# Revit family: Hafa Shower corner IglooPro Corner all sizes
name_source: partatom
category: Generic Models
units: mm (PartAtom-declared; Revit-internal decimal feet)

## family parameters
Always vertical = Yes
Can host rebar = No
Cut with Voids When Loaded = No
Part Type = Normal
Room Calculation Point = No
Round Connector Dimension = Use Diameter
Shared = No
Work Plane-Based = No

## types (32) — shared parameters
Description = Shower corner
ETIM class = EC010034
Manufacturer = Hafa Bathroom Group
Profile and Handle material = Aluminium
URL = https://www.hafa.se

## per-type parameters (varying)
| type | Doorblade length | Doorblade width | Glass Type | Length | Width |
| 1450411 IglooPro Corner 90x90 Clear | 816 mm | 816 mm | Glass Clear | 900 mm  [stored 2.95276 ft] | 900 mm  [stored 2.95276 ft] |
| 1450410 IglooPro Corner 80x80 Clear | 716 mm | 716 mm | Glass Clear | 800 mm  [stored 2.62467 ft] | 800 mm  [stored 2.62467 ft] |
| 1450430 IglooPro Corner 70x70 Clear | 616 mm | 616 mm | Glass Clear | 700 mm  [stored 2.29659 ft] | 700 mm  [stored 2.29659 ft] |
| 1450431 IglooPro Corner 70x80 Clear | 616 mm | 716 mm | Glass Clear | 700 mm  [stored 2.29659 ft] | 800 mm  [stored 2.62467 ft] |
| 1450431 IglooPro Corner 80x70 Clear | 716 mm | 616 mm | Glass Clear | 800 mm  [stored 2.62467 ft] | 700 mm  [stored 2.29659 ft] |
| 1450432 IglooPro Corner 70x90 Clear | 816 mm | 616 mm | Glass Clear | 900 mm  [stored 2.95276 ft] | 700 mm  [stored 2.29659 ft] |
| 1450432 IglooPro Corner 90x70 Clear | 616 mm | 816 mm | Glass Clear | 700 mm  [stored 2.29659 ft] | 900 mm  [stored 2.95276 ft] |
| 1450433 IglooPro Corner 70x100 Clear | 616 mm | 916 mm  [stored 3.00525 ft] | Glass Clear | 700 mm  [stored 2.29659 ft] | 1000 mm  [stored 3.28084 ft] |
| 1450433 IglooPro Corner 100x70 Clear | 916 mm  [stored 3.00525 ft] | 616 mm | Glass Clear | 1000 mm  [stored 3.28084 ft] | 700 mm  [stored 2.29659 ft] |
| 1450434 IglooPro Corner 80x90 Clear | 716 mm | 816 mm | Glass Clear | 800 mm  [stored 2.62467 ft] | 900 mm  [stored 2.95276 ft] |
| 1450434 IglooPro Corner 90x80 Clear | 816 mm | 716 mm | Glass Clear | 900 mm  [stored 2.95276 ft] | 800 mm  [stored 2.62467 ft] |
| 1450435 IglooPro Corner 80x100 Clear | 716 mm | 916 mm  [stored 3.00525 ft] | Glass Clear | 800 mm  [stored 2.62467 ft] | 1000 mm  [stored 3.28084 ft] |
| 1450435 IglooPro Corner 100x80 Clear | 916 mm  [stored 3.00525 ft] | 716 mm | Glass Clear | 1000 mm  [stored 3.28084 ft] | 800 mm  [stored 2.62467 ft] |
| 1450436 IglooPro Corner 90x100 Clear | 816 mm | 916 mm  [stored 3.00525 ft] | Glass Clear | 900 mm  [stored 2.95276 ft] | 1000 mm  [stored 3.28084 ft] |
| 1450436 IglooPro Corner 100x90 Clear | 916 mm  [stored 3.00525 ft] | 816 mm | Glass Clear | 1000 mm  [stored 3.28084 ft] | 900 mm  [stored 2.95276 ft] |
| 1450437 IglooPro Corner 100x100 Clear | 916 mm  [stored 3.00525 ft] | 916 mm  [stored 3.00525 ft] | Glass Clear | 1000 mm  [stored 3.28084 ft] | 1000 mm  [stored 3.28084 ft] |
| 1450440 IglooPro Corner 70x70 Frost | 616 mm | 616 mm | Glass Frosted | 700 mm  [stored 2.29659 ft] | 700 mm  [stored 2.29659 ft] |
| 1450441 IglooPro Corner 70x80 Frost | 616 mm | 716 mm | Glass Frosted | 700 mm  [stored 2.29659 ft] | 800 mm  [stored 2.62467 ft] |
| 1450441 IglooPro Corner 80x70 Frost | 716 mm | 616 mm | Glass Frosted | 800 mm  [stored 2.62467 ft] | 700 mm  [stored 2.29659 ft] |
| 1450442 IglooPro Corner 70x90 Frost | 616 mm | 816 mm | Glass Frosted | 700 mm  [stored 2.29659 ft] | 900 mm  [stored 2.95276 ft] |
| 1450442 IglooPro Corner 90x70 Frost | 816 mm | 616 mm | Glass Frosted | 900 mm  [stored 2.95276 ft] | 700 mm  [stored 2.29659 ft] |
| 1450443 IglooPro Corner 70x100 Frost | 616 mm | 916 mm  [stored 3.00525 ft] | Glass Frosted | 700 mm  [stored 2.29659 ft] | 1000 mm  [stored 3.28084 ft] |
| 1450443 IglooPro Corner 100x70 Frost | 916 mm  [stored 3.00525 ft] | 616 mm | Glass Frosted | 1000 mm  [stored 3.28084 ft] | 700 mm  [stored 2.29659 ft] |
| 1450444 IglooPro Corner 80x80 Frost | 716 mm | 716 mm | Glass Frosted | 800 mm  [stored 2.62467 ft] | 800 mm  [stored 2.62467 ft] |
| 1450445 IglooPro Corner 80x90 Frost | 716 mm | 816 mm | Glass Frosted | 800 mm  [stored 2.62467 ft] | 900 mm  [stored 2.95276 ft] |
| 1450445 IglooPro Corner 90x80 Frost | 816 mm | 716 mm | Glass Frosted | 900 mm  [stored 2.95276 ft] | 800 mm  [stored 2.62467 ft] |
| 1450446 IglooPro Corner 80x100 Frost | 716 mm | 916 mm  [stored 3.00525 ft] | Glass Frosted | 800 mm  [stored 2.62467 ft] | 1000 mm  [stored 3.28084 ft] |
| 1450446 IglooPro Corner 100x80 Frost | 916 mm  [stored 3.00525 ft] | 716 mm | Glass Frosted | 1000 mm  [stored 3.28084 ft] | 800 mm  [stored 2.62467 ft] |
| 1450447 IglooPro Corner 90x90 Frost | 816 mm | 816 mm | Glass Frosted | 900 mm  [stored 2.95276 ft] | 900 mm  [stored 2.95276 ft] |
| 1450448 IglooPro Corner 90x100 Frost | 816 mm | 916 mm  [stored 3.00525 ft] | Glass Frosted | 900 mm  [stored 2.95276 ft] | 1000 mm  [stored 3.28084 ft] |
| 1450448 IglooPro Corner 100x90 Frost | 916 mm  [stored 3.00525 ft] | 816 mm | Glass Frosted | 1000 mm  [stored 3.28084 ft] | 900 mm  [stored 2.95276 ft] |
| 1450449 IglooPro Corner 100x100 Frost | 916 mm  [stored 3.00525 ft] | 916 mm  [stored 3.00525 ft] | Glass Frosted | 1000 mm  [stored 3.28084 ft] | 1000 mm  [stored 3.28084 ft] |

note: [stored X ft] marks values corroborated as IEEE doubles in the binary element streams (Revit-internal decimal feet)

## geometry (parser evidence)
native form markers: Sweep x2
no freeform markers — native parametric forms only
